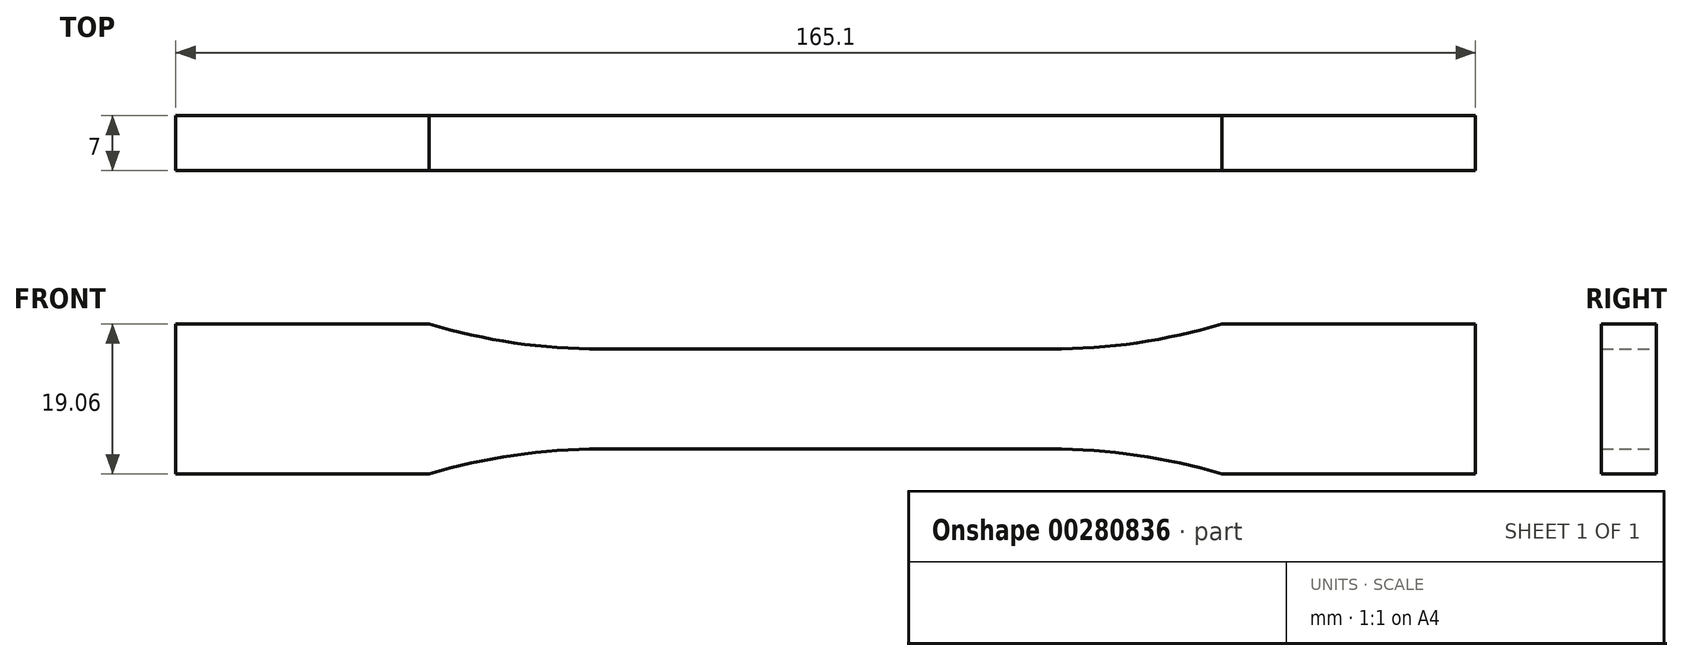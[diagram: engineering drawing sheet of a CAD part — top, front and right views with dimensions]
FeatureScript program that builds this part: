
annotation { "Feature Type Name" : "Feature", "Feature Type Description" : "" }
export const myFeature = defineFeature(function(context is Context, id is Id, definition is map)
    precondition{}
    {
        {
            var Q0;
            Q0=qCreatedBy(makeId("Front.planeOp"),FACE);
            var sketch = newSketch(context, id + "F0", { "sketchPlane" : qUnion([Q0])});
            skLineSegment(sketch, "E0", {"start": v(0, 6.35) * mm, "end": v(28.58, 6.35) * mm});
            skArc(sketch, "E1", {"start": v(28.58, 6.35) * mm, "mid": v(39.57, 7.15) * mm, "end": v(50.34, 9.52) * mm});
            skLineSegment(sketch, "E2", {"start": v(50.34, 9.53) * mm, "end": v(82.55, 9.53) * mm});
            skLineSegment(sketch, "E3", {"start": v(82.55, 9.52) * mm, "end": v(82.55, 0) * mm});
            skArc(sketch, "E4.MirrorCS", {"start": v(28.58, -6.35) * mm, "mid": v(39.57, -7.15) * mm, "end": v(50.34, -9.52) * mm});
            skLineSegment(sketch, "E5.MirrorCS", {"start": v(0, -6.35) * mm, "end": v(28.58, -6.35) * mm});
            skLineSegment(sketch, "E6.MirrorCS", {"start": v(82.55, -9.52) * mm, "end": v(82.55, 0) * mm});
            skLineSegment(sketch, "E7.MirrorCS", {"start": v(50.34, -9.52) * mm, "end": v(82.55, -9.52) * mm});
            skLineSegment(sketch, "E8.MirrorCS", {"start": v(-50.34, -9.52) * mm, "end": v(-82.55, -9.52) * mm});
            skLineSegment(sketch, "E9.MirrorCS", {"start": v(-82.55, -9.52) * mm, "end": v(-82.55, 0) * mm});
            skLineSegment(sketch, "E10.MirrorCS", {"start": v(0, -6.35) * mm, "end": v(-28.58, -6.35) * mm});
            skLineSegment(sketch, "E11.MirrorCS", {"start": v(-82.55, 9.52) * mm, "end": v(-82.55, 0) * mm});
            skArc(sketch, "E12.MirrorCS", {"start": v(-28.58, 6.35) * mm, "mid": v(-39.57, 7.15) * mm, "end": v(-50.34, 9.52) * mm});
            skLineSegment(sketch, "E13.MirrorCS", {"start": v(-50.34, 9.53) * mm, "end": v(-82.55, 9.53) * mm});
            skLineSegment(sketch, "E14.MirrorCS", {"start": v(0, 6.35) * mm, "end": v(-28.58, 6.35) * mm});
            skArc(sketch, "E15.MirrorCS", {"start": v(-28.58, -6.35) * mm, "mid": v(-39.57, -7.15) * mm, "end": v(-50.34, -9.52) * mm});
            skSolve(sketch);
        }
        {
            var Q0;
            Q0=makeQuery(id+"F0.imprint","IMPRINT",FACE,{"disambiguationData":[TD([[makeQuery(id+"F0.imprint","IMPRINT",EDGE,{"derivedFrom":sQuery(id+"F0.wireOp",EDGE,"E0")}),-1.0]])]});
            extrude(context, id + "F1", {"entities" : qUnion([Q0]), "endBound" : BoundingType.SYMMETRIC, "depth" : 7 * mm});
        }
    });
